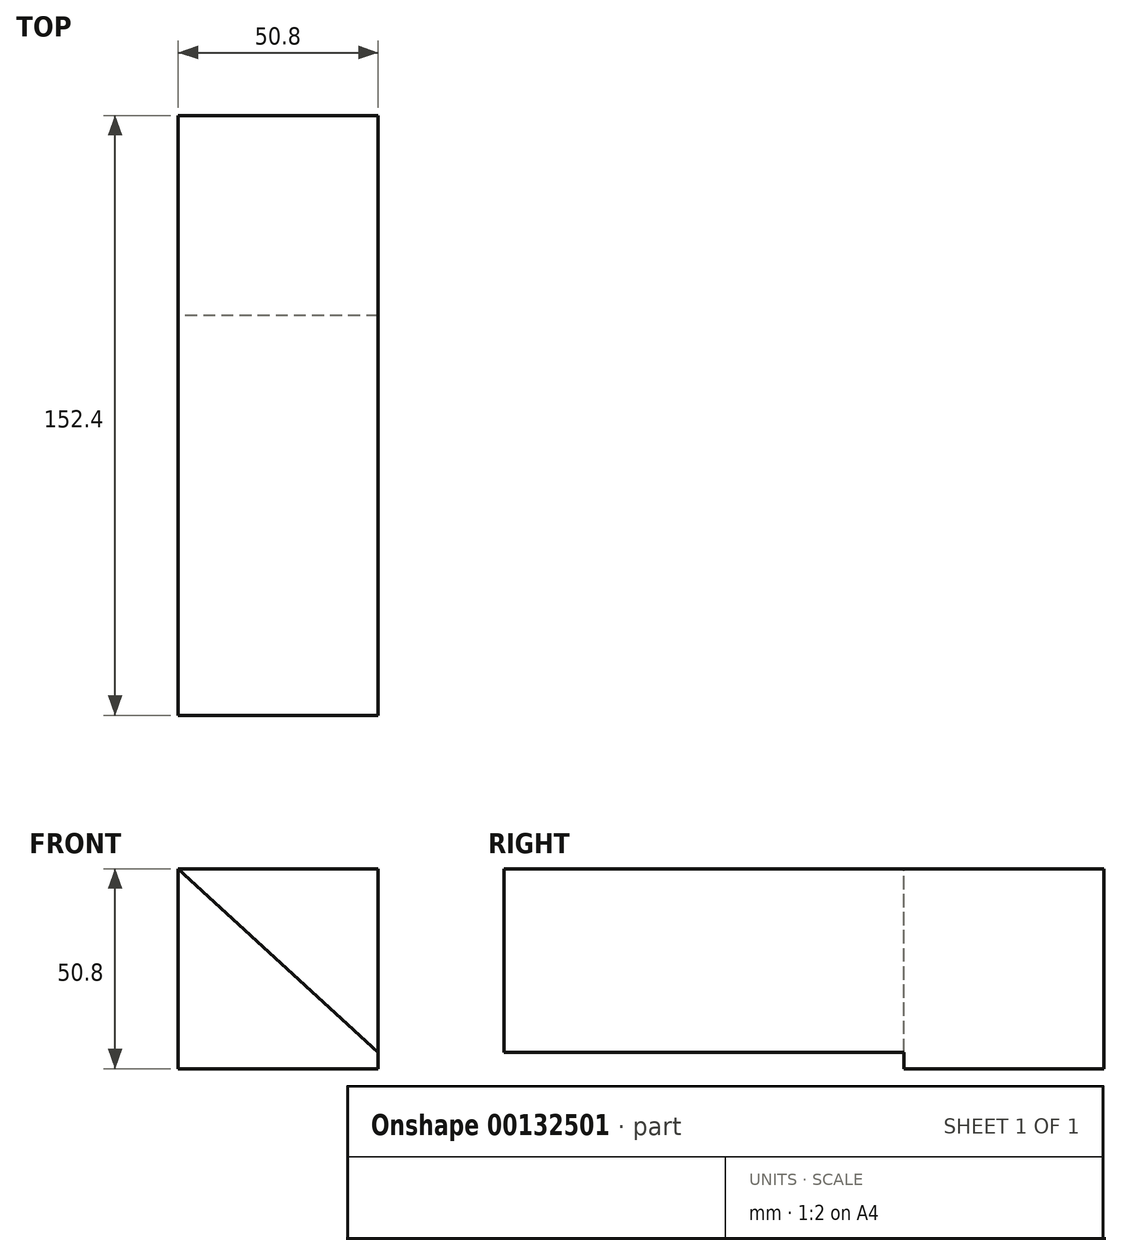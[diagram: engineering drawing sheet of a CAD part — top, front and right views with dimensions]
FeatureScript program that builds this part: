
annotation { "Feature Type Name" : "Feature", "Feature Type Description" : "" }
export const myFeature = defineFeature(function(context is Context, id is Id, definition is map)
    precondition{}
    {
        {
            var Q0;
            Q0=qCreatedBy(makeId("Front.planeOp"),FACE);
            var sketch = newSketch(context, id + "F0", { "sketchPlane" : qUnion([Q0])});
            skLineSegment(sketch, "E0.bottom", {"start": v(0, 0) * mm, "end": v(50.8, 0) * mm});
            skLineSegment(sketch, "E0.top", {"start": v(0, 50.8) * mm, "end": v(50.8, 50.8) * mm});
            skLineSegment(sketch, "E0.left", {"start": v(0, 0) * mm, "end": v(0, 50.8) * mm});
            skLineSegment(sketch, "E0.right", {"start": v(50.8, 0) * mm, "end": v(50.8, 50.8) * mm});
            skSolve(sketch);
        }
        {
            var Q0;
            Q0=makeQuery(id+"F0.imprint","IMPRINT",FACE,{"disambiguationData":[TD([[makeQuery(id+"F0.imprint","IMPRINT",EDGE,{"derivedFrom":sQuery(id+"F0.wireOp",EDGE,"E0.bottom")}),1.0]])]});
            extrude(context, id + "F1", {"entities" : qUnion([Q0]), "depth" : 50.8 * mm});
        }
        {
            var Q0;
            Q0=makeQuery(id+"F1.opExtrude","CAP_FACE",FACE,{"disambiguationData":[OSD([sQuery(id+"F0.wireOp",EDGE,"E0.bottom"),sQuery(id+"F0.wireOp",EDGE,"E0.top"),sQuery(id+"F0.wireOp",EDGE,"E0.left"),sQuery(id+"F0.wireOp",EDGE,"E0.right")])],"isStart":false});
            var sketch = newSketch(context, id + "F2", { "sketchPlane" : qUnion([Q0])});
            skLineSegment(sketch, "E1", {"start": v(50.8, 50.8) * mm, "end": v(50.8, 4.2) * mm});
            skLineSegment(sketch, "E2", {"start": v(50.8, 4.2) * mm, "end": v(0, 50.8) * mm});
            skSolve(sketch);
        }
        {
            var Q0;
            Q0=makeQuery(id+"F2.imprint","IMPRINT",FACE,{"disambiguationData":[TD([[makeQuery(id+"F2.imprint","IMPRINT",EDGE,{"derivedFrom":sQuery(id+"F2.wireOp",EDGE,"E1")}),1.0]])]});
            extrude(context, id + "F3", {"entities" : qUnion([Q0]), "operationType" : NewBodyOperationType.ADD, "depth" : 101.6 * mm});
        }
    });
